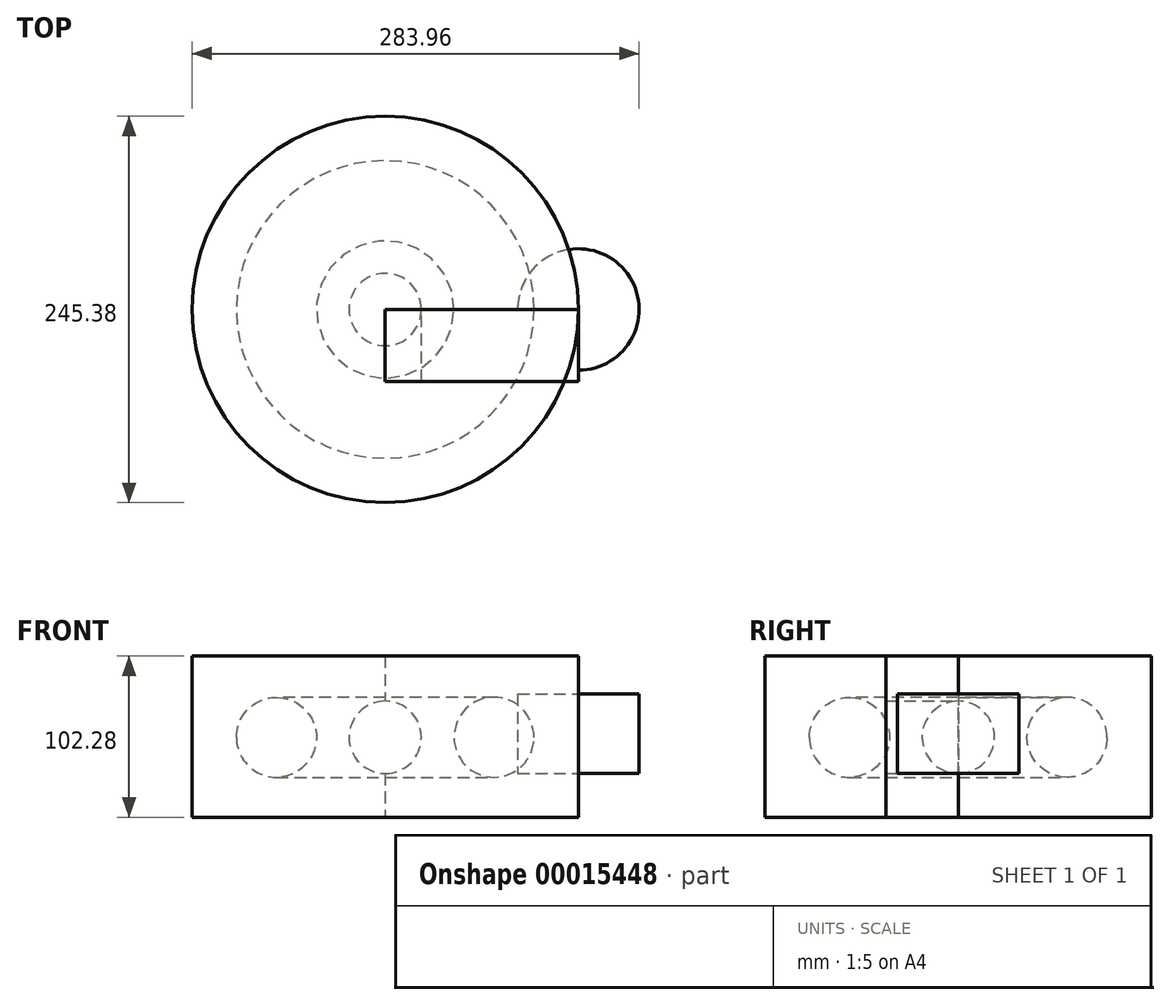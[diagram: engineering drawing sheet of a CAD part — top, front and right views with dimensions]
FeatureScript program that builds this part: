
annotation { "Feature Type Name" : "Feature", "Feature Type Description" : "" }
export const myFeature = defineFeature(function(context is Context, id is Id, definition is map)
    precondition{}
    {
        {
            var Q0;
            Q0=qCreatedBy(makeId("Front.planeOp"),FACE);
            var sketch = newSketch(context, id + "F0", { "sketchPlane" : qUnion([Q0])});
            skCircle(sketch, "E0", {"center": v(0, 0) * mm, "radius": 25.4 * mm});
            skLineSegment(sketch, "E1.bottom", {"start": v(-69.1, 51.55) * mm, "end": v(53.6, 51.55) * mm});
            skLineSegment(sketch, "E1.top", {"start": v(-69.1, -50.73) * mm, "end": v(53.6, -50.73) * mm});
            skLineSegment(sketch, "E1.left", {"start": v(-69.1, 51.55) * mm, "end": v(-69.1, -50.73) * mm});
            skLineSegment(sketch, "E1.right", {"start": v(53.6, 51.55) * mm, "end": v(53.6, -50.73) * mm});
            skLineSegment(sketch, "E2.bottom", {"start": v(53.6, -22.86) * mm, "end": v(92.17, -22.86) * mm});
            skLineSegment(sketch, "E2.top", {"start": v(53.6, 27.66) * mm, "end": v(92.17, 27.66) * mm});
            skLineSegment(sketch, "E2.left", {"start": v(53.6, -22.86) * mm, "end": v(53.6, 27.66) * mm});
            skLineSegment(sketch, "E2.right", {"start": v(92.17, -22.86) * mm, "end": v(92.17, 27.66) * mm});
            skCircle(sketch, "E3", {"center": v(-69.1, 0) * mm, "radius": 22.99 * mm});
            skSolve(sketch);
        }
        {
            var Q0;
            Q0=makeQuery(id+"F0.imprint","IMPRINT",FACE,{"disambiguationData":[TD([[makeQuery(id+"F0.imprint","IMPRINT",EDGE,{"derivedFrom":sQuery(id+"F0.wireOp",EDGE,"E0")}),-1.0]])]});
            var Q1;
            Q1=makeQuery(id+"F0.imprint","IMPRINT",FACE,{"disambiguationData":[TD([[makeQuery(id+"F0.imprint","IMPRINT",EDGE,{"derivedFrom":sQuery(id+"F0.wireOp",EDGE,"E0")}),1.0]])]});
            extrude(context, id + "F1", {"entities" : qUnion([Q0, Q1]), "depth" : 45.77 * mm});
        }
        {
            var Q0;
            Q0=makeQuery(id+"F0.imprint","IMPRINT",FACE,{"disambiguationData":[TD([[makeQuery(id+"F0.imprint","IMPRINT",EDGE,{"derivedFrom":sQuery(id+"F0.wireOp",EDGE,"E2.bottom")}),1.0]])]});
            var Q1;
            Q1=sQuery(id+"F0.wireOp",EDGE,"E2.left");
            revolve(context, id + "F2", {"operationType" : NewBodyOperationType.ADD, "entities" : qUnion([Q0]), "axis" : qUnion([Q1]), "revolveType" : RevolveType.FULL});
        }
        {
            var Q0;
            {var subQ0=sQuery(id+"F0.wireOp",EDGE,"E3");var subQ1=sQuery(id+"F0.wireOp",EDGE,"E1.left");var subQ3=makeQuery(id+"F0.imprint","INTERSECT",VERTEX,{"disambiguationData":[OD(0.0)],"derivedFrom":[subQ1,subQ0]});Q0=makeQuery(id+"F0.imprint","IMPRINT",FACE,{"disambiguationData":[TD([[makeQuery(id+"F0.imprint","IMPRINT",EDGE,{"disambiguationData":[TD([[subQ3,-1.0]])],"derivedFrom":subQ1}),1.0]])]});}
            var Q1;
            Q1=sQuery(id+"F0.wireOp",EDGE,"E1.left");
            revolve(context, id + "F3", {"entities" : qUnion([Q0]), "axis" : qUnion([Q1]), "revolveType" : RevolveType.FULL});
        }
    });
